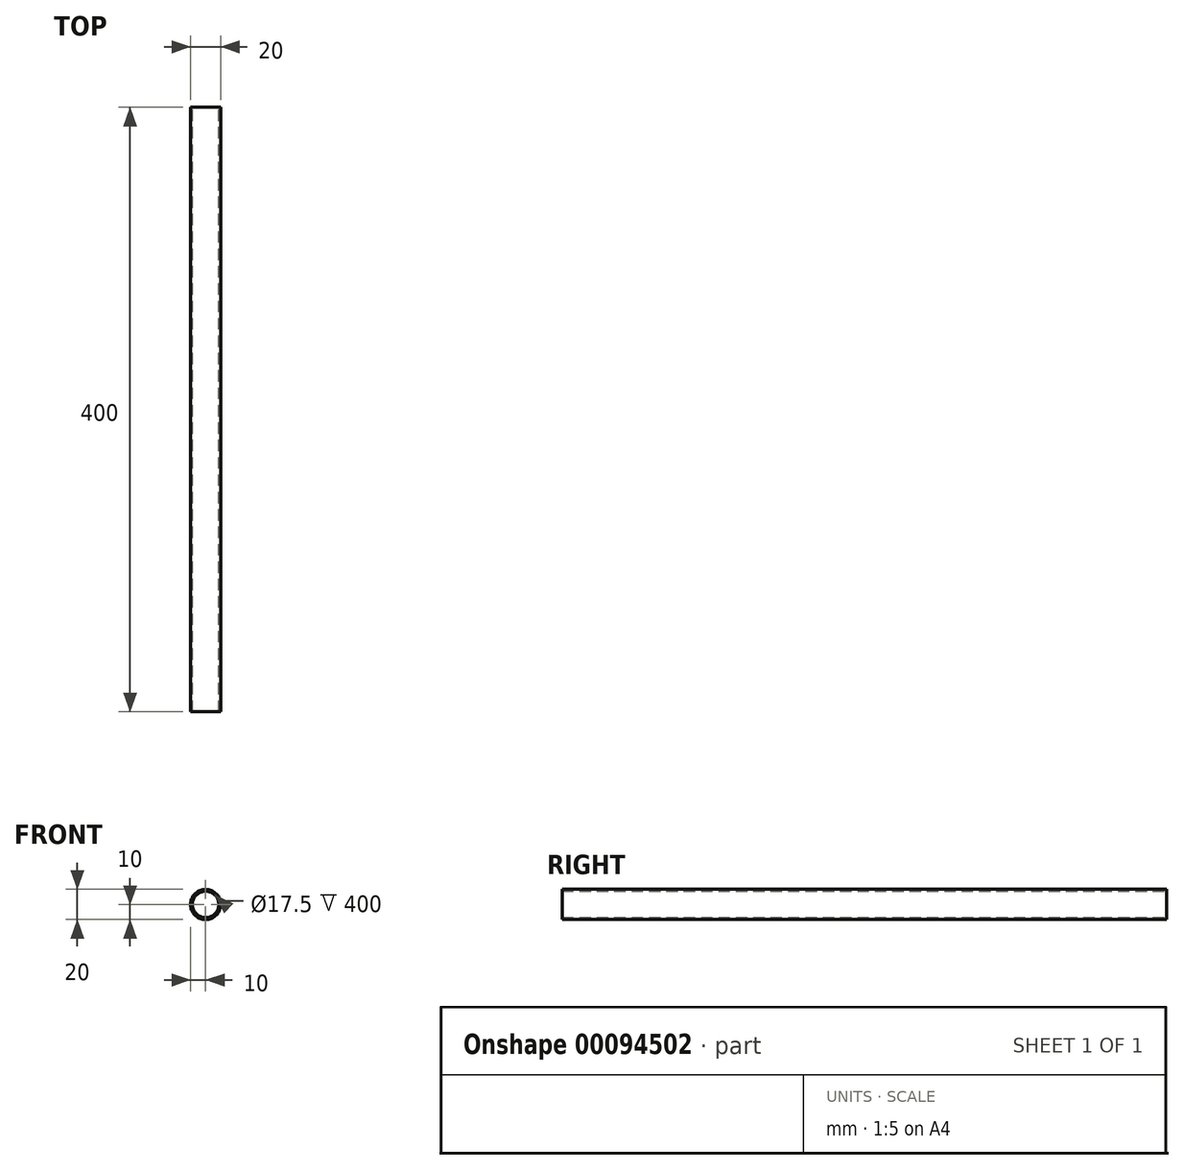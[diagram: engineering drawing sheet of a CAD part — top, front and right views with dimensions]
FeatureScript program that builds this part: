
annotation { "Feature Type Name" : "Feature", "Feature Type Description" : "" }
export const myFeature = defineFeature(function(context is Context, id is Id, definition is map)
    precondition{}
    {
        {
            var Q0;
            Q0=qCreatedBy(makeId("Front.planeOp"),FACE);
            var sketch = newSketch(context, id + "F0", { "sketchPlane" : qUnion([Q0])});
            skCircle(sketch, "E0", {"center": v(0, 0) * mm, "radius": 10 * mm});
            skCircle(sketch, "E1", {"center": v(0, 0) * mm, "radius": 8.75 * mm});
            skSolve(sketch);
        }
        {
            var Q0;
            Q0 = qSketchRegion(id + "F0", true);
            extrude(context, id + "F1", {"entities" : qUnion([Q0]), "depth" : 400 * mm});
        }
    });
